# Revit family: Турникет трипод PERCo_TTR-10
name_source: partatom
category: Оборудование
units: mm (PartAtom-declared; Revit-internal decimal feet)

## family parameters
Всегда вертикально = Нет
Классификация = Нет
На основе рабочей плоскости = Нет
Общий = Нет
При загрузке вырезать с полостями = Нет
Размер круглого соединителя = Использовать диаметр
Тип детали = Нормальный
Точка расчета площади = Нет

## types (2) — shared parameters
ADSK_URL страницы изделия = https://www.perco.ru
ADSK_Единица измерения = шт.
ADSK_Завод-изготовитель = PERCo
ADSK_Количество = 1
ADSK_Материал наименование = Корпус турникета и планки выполнены из высококачественной нержавеющей стали
ADSK_Напряжение = 24 В
ADSK_Номинальная мощность = 150 Вт
ADSK_Ток = 6 А
Встраивание считывателей внутрь = Не предусмотрено
Габаритные размеры контроллера для встраивания в нишу = Не предусмотрено
Габаритные размеры считывателя для встраивания в ниши = Не предусмотрено
Длина планки = 539 мм
Корпус = Нержавейка
Напольное крепление_каркас = Нержавейка
Напольное крепление_покрытие = панель
Основа планки = Черный
Планки = Нержавейка
Подключение к электросети = 220 В
Пропускная способность = 30 чел./мин
Степень защиты оболочки = IP54
Температура использования = от -40°С до +50°С
Цвет = нержавейка
Ширина зоны прохода = 500 мм.

## per-type parameters (varying)
| type | ADSK_Масса_Текст | ADSK_Наименование | ADSK_Наименование краткое | Габаритные размеры (длина×ширина×высота) | Напольное крепление |
| TTR-10AB | не более 33 кг | Турникет моторизованный PERCo-TTR-10АB всепогодный с автоматическими планками «Антипаника» | Турникет TTR-10АB | 1055×800×760 мм | Да |
| TTR-10AK | не более 55кг | Турникет моторизованный PERCo-TTR-10АK всепогодный с автоматическими планками «Антипаника» | Турникет TTR-10АK | 613×800×714 мм | Нет |
